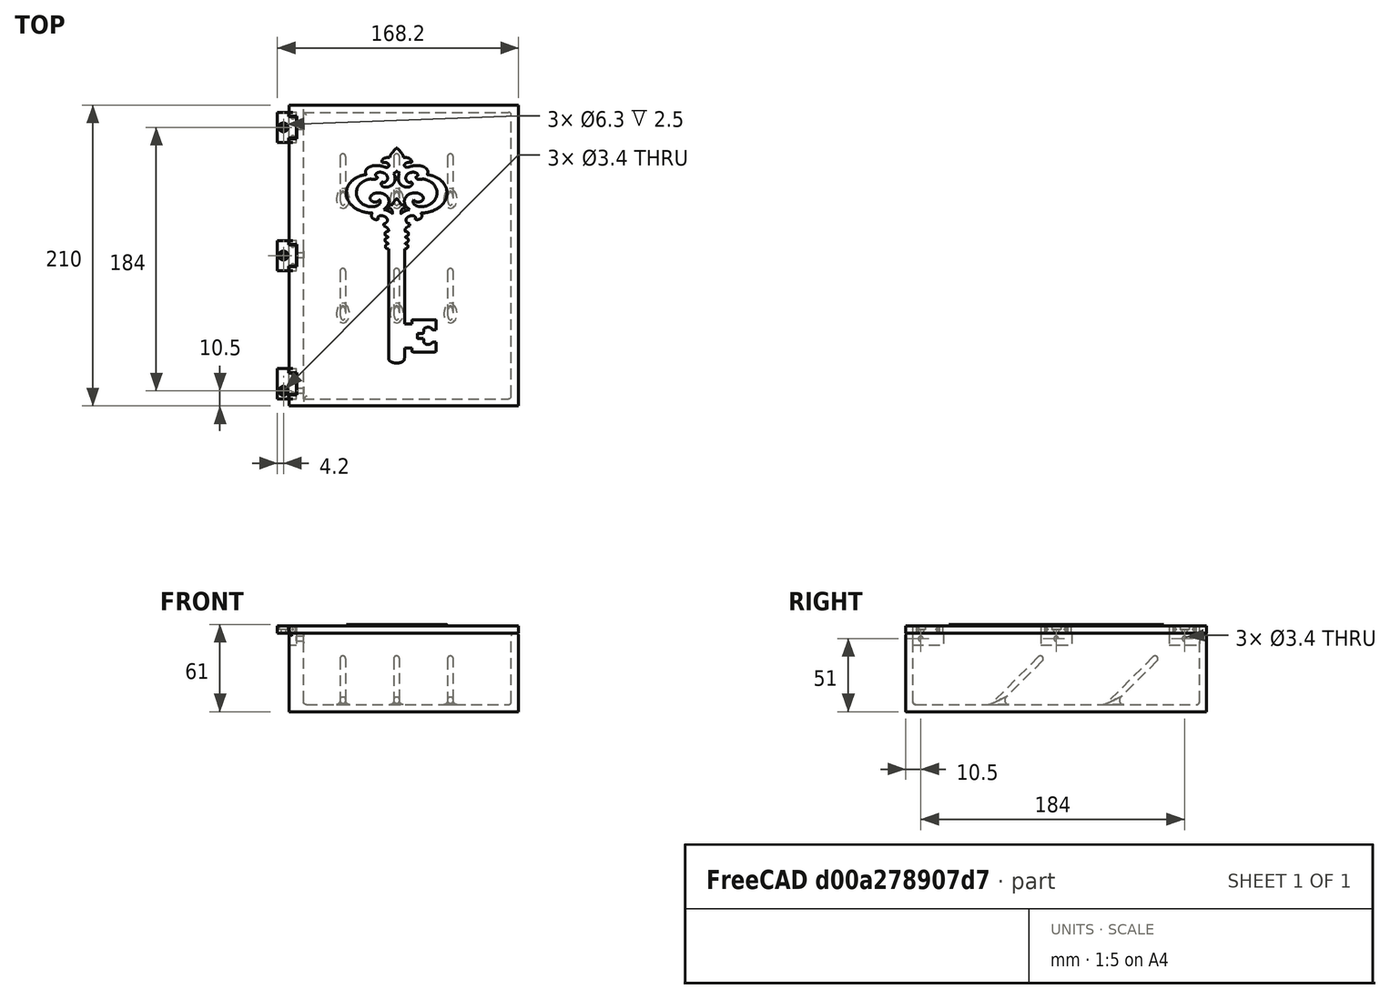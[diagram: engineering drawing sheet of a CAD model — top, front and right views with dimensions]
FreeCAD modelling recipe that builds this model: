
FCSTD DOCUMENT  (FreeCAD 1.1R1.1.0)
Label: SimpleCabinet
License: All rights reserved
LicenseURL: http://en.wikipedia.org/wiki/All_rights_reserved
objects: Part::MultiFuse×29, Part::Box×27, Part::Cylinder×24, Part::Cut×17, Part::Cone×12, Part::Fillet×4, Spreadsheet::Sheet×2, Part::Feature×1, App::Point×1, PartDesign::FeatureBase×1, PartDesign::Pad×1, PartDesign::Body×1
note: 120 computed .brp shape members not serialized (recipe doc carries the construction recipe); baked Part::Feature solids carry a one-line shape summary decoded from their .brp

FEATURE [Part::Box] Box  label="Cube"
  AttacherType = Attacher::AttachEngine3D
  Height = 50
  Length = 145
  Placement = pos=(10,5,5) rot=(0,0,1;0rad)
  Width = 200
  expr: .Placement.Base.x = <<Cabinet>>.wallthickness * 2
  expr: .Placement.Base.y = <<Cabinet>>.wallthickness
  expr: .Placement.Base.z = <<Cabinet>>.wallthickness
  expr: Height = <<Cabinet>>.depth
  expr: Length = <<Cabinet>>.width - <<Cabinet>>.wallthickness
  expr: Width = <<Cabinet>>.height
FEATURE [Spreadsheet::Sheet] Spreadsheet  label="Cabinet"
  cells = A2='Height; B2(height)=200; A3='Width; B3(width)=150; A4='Depth; B4(depth)=50; A5='Wall thickness; B5(wallthickness)=5
FEATURE [Part::Box] Box001  label="Cube001"
  AttacherType = Attacher::AttachEngine3D
  Height = 55
  Length = 160
  Width = 210
  expr: Height = <<Cabinet>>.depth + 1 * <<Cabinet>>.wallthickness
  expr: Length = <<Cabinet>>.width + 2 * <<Cabinet>>.wallthickness
  expr: Width = <<Cabinet>>.height + 2 * <<Cabinet>>.wallthickness
FEATURE [Part::Cut] Cut
  Base = -> Box001
  Tool = -> Box
FEATURE [Part::Box] Box002  label="Cube002"
  AttacherType = Attacher::AttachEngine3D
  Height = 5
  Length = 160
  Placement = pos=(0,0,55) rot=(0,0,1;0rad)
  Width = 210
  expr: .Placement.Base.z = <<Cabinet>>.depth + <<Cabinet>>.wallthickness
  expr: Height = <<Cabinet>>.wallthickness
  expr: Length = <<Cabinet>>.width + 2 * <<Cabinet>>.wallthickness
  expr: Width = <<Cabinet>>.height + 2 * <<Cabinet>>.wallthickness
FEATURE [Part::Box] Box003  label="Cube003"
  AttacherType = Attacher::AttachEngine3D
  Height = 5
  Length = 21
  Width = 10.9
  expr: Height = <<HingeParams>>.thickness
  expr: Length = <<HingeParams>>.h1 + <<HingeParams>>.h2
  expr: Width = <<HingeParams>>.e1 + <<HingeParams>>.thickness / 2 + <<HingeParams>>.gap
FEATURE [Part::Box] Box004  label="Cube004"
  AttacherType = Attacher::AttachEngine3D
  Height = 5
  Length = 15.8
  Placement = pos=(2.6,8,0) rot=(0,0,1;0rad)
  Width = 5.8
  expr: .Placement.Base.x = <<HingeParams>>.h2 / 2 - <<HingeParams>>.gap
  expr: .Placement.Base.y = <<HingeParams>>.e1
  expr: Height = <<HingeParams>>.thickness
  expr: Length = <<HingeParams>>.h1 + 2 * <<HingeParams>>.gap
  expr: Width = <<HingeParams>>.thickness + 2 * <<HingeParams>>.gap
FEATURE [Part::Box] Box005  label="Cube005"
  AttacherType = Attacher::AttachEngine3D
  Height = 5
  Length = 15
  Placement = pos=(3,10.9,0) rot=(0,0,1;0rad)
  Width = 10.5
  expr: .Placement.Base.x = <<HingeParams>>.h2 / 2
  expr: .Placement.Base.y = <<HingeParams>>.e1 + <<HingeParams>>.gap + <<HingeParams>>.thickness / 2
  expr: Height = <<HingeParams>>.thickness
  expr: Length = <<HingeParams>>.h1
  expr: Width = <<HingeParams>>.thickness / 2 + <<HingeParams>>.e2
FEATURE [Part::Box] Box006  label="Cube006"
  AttacherType = Attacher::AttachEngine3D
  Height = 5
  Length = 21
  Placement = pos=(0,13.8,0) rot=(0,0,1;0rad)
  Width = 7.8
  expr: .Placement.Base.y = <<HingeParams>>.e1 + <<HingeParams>>.thickness + <<HingeParams>>.gap * 2
  expr: Height = <<HingeParams>>.thickness
  expr: Length = <<HingeParams>>.h1 + <<HingeParams>>.h2
  expr: Width = <<HingeParams>>.e2 - <<HingeParams>>.gap / 2
FEATURE [Part::Cone] Cone
  Angle = 360
  AttacherType = Attacher::AttachEngine3D
  Height = 1.6
  Placement = pos=(4.2,10.9,2.5) rot=(0,1,0;-1.5708rad)
  Radius1 = 0.5
  Radius2 = 2.1
  expr: .Placement.Base.x = <<HingeParams>>.h2 / 2 - <<HingeParams>>.gap + <<HingeParams>>.thickness / 2 - <<HingeParams>>.gap - 0.5
  expr: .Placement.Base.y = <<HingeParams>>.e1 + <<HingeParams>>.gap + <<HingeParams>>.thickness / 2
  expr: .Placement.Base.z = <<HingeParams>>.thickness / 2
  expr: Height = <<HingeParams>>.thickness / 2 - <<HingeParams>>.gap - 0.5
  expr: Radius1 = 0.5
  expr: Radius2 = <<HingeParams>>.thickness / 2 - <<HingeParams>>.gap
FEATURE [Part::Cone] Cone002
  Angle = 360
  AttacherType = Attacher::AttachEngine3D
  Height = 2
  Placement = pos=(4.6,10.9,2.5) rot=(0,1,0;-1.5708rad)
  Radius1 = 0.5
  Radius2 = 2.5
  expr: .Placement.Base.x = <<HingeParams>>.h2 / 2 + <<HingeParams>>.thickness / 2 - <<HingeParams>>.gap - 0.5
  expr: .Placement.Base.y = <<HingeParams>>.e1 + <<HingeParams>>.gap + <<HingeParams>>.thickness / 2
  expr: .Placement.Base.z = <<HingeParams>>.thickness / 2
  expr: Height = <<HingeParams>>.thickness / 2 - 0.5
  expr: Radius1 = 0.5
  expr: Radius2 = <<HingeParams>>.thickness / 2
FEATURE [Part::Cone] Cone003
  Angle = 360
  AttacherType = Attacher::AttachEngine3D
  Height = 1.6
  Placement = pos=(16.8,10.9,2.5) rot=(0,1,0;1.5708rad)
  Radius1 = 0.5
  Radius2 = 2.1
  expr: .Placement.Base.x = <<HingeParams>>.h1 + <<HingeParams>>.h2 / 2 - (<<HingeParams>>.thickness / 2 - <<HingeParams>>.gap - 0.5) + <<HingeParams>>.gap
  expr: .Placement.Base.y = <<HingeParams>>.e1 + <<HingeParams>>.gap + <<HingeParams>>.thickness / 2
  expr: .Placement.Base.z = <<HingeParams>>.thickness / 2
  expr: Height = <<HingeParams>>.thickness / 2 - <<HingeParams>>.gap - 0.5
  expr: Radius1 = 0.5
  expr: Radius2 = <<HingeParams>>.thickness / 2 - <<HingeParams>>.gap
FEATURE [Part::Cone] Cone004
  Angle = 360
  AttacherType = Attacher::AttachEngine3D
  Height = 2
  Placement = pos=(16.4,10.9,2.5) rot=(0,1,0;1.5708rad)
  Radius1 = 0.5
  Radius2 = 2.5
  expr: .Placement.Base.x = <<HingeParams>>.h1 + <<HingeParams>>.h2 / 2 - (<<HingeParams>>.thickness / 2 - <<HingeParams>>.gap - 0.5)
  expr: .Placement.Base.y = <<HingeParams>>.e1 + <<HingeParams>>.gap + <<HingeParams>>.thickness / 2
  expr: .Placement.Base.z = <<HingeParams>>.thickness / 2
  expr: Height = <<HingeParams>>.thickness / 2 - 0.5
  expr: Radius1 = 0.5
  expr: Radius2 = <<HingeParams>>.thickness / 2
FEATURE [Part::Cylinder] Cylinder
  Angle = 360
  AttacherType = Attacher::AttachEngine3D
  FirstAngle = 0
  Height = 21
  Placement = pos=(0,10.9,2.5) rot=(0,1,0;1.5708rad)
  Radius = 2.5
  SecondAngle = 0
  expr: .Placement.Base.y = <<HingeParams>>.e1 + <<HingeParams>>.gap + <<HingeParams>>.thickness / 2
  expr: .Placement.Base.z = <<HingeParams>>.thickness / 2
  expr: Height = <<HingeParams>>.h1 + <<HingeParams>>.h2
  expr: Radius = <<HingeParams>>.thickness / 2
FEATURE [Part::Cylinder] Cylinder001
  Angle = 360
  AttacherType = Attacher::AttachEngine3D
  FirstAngle = 0
  Height = 15
  Placement = pos=(3,10.9,2.5) rot=(0,1,0;1.5708rad)
  Radius = 2.5
  SecondAngle = 0
  expr: .Placement.Base.x = <<HingeParams>>.h2 / 2
  expr: .Placement.Base.y = <<HingeParams>>.e1 + <<HingeParams>>.gap + <<HingeParams>>.thickness / 2
  expr: .Placement.Base.z = <<HingeParams>>.thickness / 2
  expr: Height = <<HingeParams>>.h1
  expr: Radius = <<HingeParams>>.thickness / 2
FEATURE [Part::MultiFuse] Fusion
  Shapes = -> [Box003,Cylinder]
FEATURE [Part::Cut] Cut001
  Base = -> Fusion
  Tool = -> Box004
FEATURE [Part::MultiFuse] Fusion001
  Shapes = -> [Cone,Cone003,Cut001]
FEATURE [Part::MultiFuse] Fusion002
  Shapes = -> [Box006,Box005,Cylinder001]
FEATURE [Part::MultiFuse] Fusion003
  Shapes = -> [Cone004,Cone002]
FEATURE [Part::Cut] Cut002
  Base = -> Fusion002
  Tool = -> Fusion003
FEATURE [Part::MultiFuse] Fusion004  label="Hinge"
  Placement = pos=(13.4,5,55) rot=(0,0,1;1.5708rad)
  Shapes = -> [Fusion001,Cut002]
  expr: .Placement.Base.x = 8 + <<Cabinet>>.wallthickness + <<HingeParams>>.gap
  expr: .Placement.Base.y = <<Cabinet>>.wallthickness
  expr: .Placement.Base.z = <<Cabinet>>.depth + <<Cabinet>>.wallthickness
FEATURE [Spreadsheet::Sheet] Spreadsheet001  label="HingeParams"
  cells = A2='Thickness; B2(thickness)==<<Cabinet>>.wallthickness; A3='Hinge length 1; B3(h1)=15; A4='Hinge length 2; B4(h2)=6; A5='Gap; B5(gap)=0.4; A6='Extend 1; B6(e1)=8; A7='Extend 2; B7(e2)=8
FEATURE [Part::Box] Box007  label="Cube007"
  AttacherType = Attacher::AttachEngine3D
  Height = 5
  Length = 13.4
  Placement = pos=(0,5,55) rot=(0,0,1;0rad)
  Width = 21
  expr: .Placement.Base.y = <<Cabinet>>.wallthickness
  expr: .Placement.Base.z = <<Cabinet>>.depth + <<Cabinet>>.wallthickness
  expr: Height = <<Cabinet>>.wallthickness
  expr: Length = 8 + <<HingeParams>>.gap + <<Cabinet>>.wallthickness
  expr: Width = <<HingeParams>>.h1 + <<HingeParams>>.h2
FEATURE [Part::Box] Box008  label="Cube008"
  AttacherType = Attacher::AttachEngine3D
  Height = 5
  Length = 13.4
  Placement = pos=(0,184,55) rot=(0,0,1;0rad)
  Width = 21
  expr: .Placement.Base.y = <<Cabinet>>.height + <<Cabinet>>.wallthickness * 2 - (<<HingeParams>>.h1 + <<HingeParams>>.h2) - <<Cabinet>>.wallthickness
  expr: .Placement.Base.z = <<Cabinet>>.depth + <<Cabinet>>.wallthickness
  expr: Height = <<Cabinet>>.wallthickness
  expr: Length = 8 + <<HingeParams>>.gap + <<Cabinet>>.wallthickness
  expr: Width = <<HingeParams>>.h1 + <<HingeParams>>.h2
FEATURE [Part::Box] Box009  label="Cube009"
  AttacherType = Attacher::AttachEngine3D
  Height = 5
  Length = 21
  Width = 10.9
  expr: Height = <<HingeParams>>.thickness
  expr: Length = <<HingeParams>>.h1 + <<HingeParams>>.h2
  expr: Width = <<HingeParams>>.e1 + <<HingeParams>>.thickness / 2 + <<HingeParams>>.gap
FEATURE [Part::Box] Box010  label="Cube010"
  AttacherType = Attacher::AttachEngine3D
  Height = 5
  Length = 15.8
  Placement = pos=(2.6,8,0) rot=(0,0,1;0rad)
  Width = 5.8
  expr: .Placement.Base.x = <<HingeParams>>.h2 / 2 - <<HingeParams>>.gap
  expr: .Placement.Base.y = <<HingeParams>>.e1
  expr: Height = <<HingeParams>>.thickness
  expr: Length = <<HingeParams>>.h1 + 2 * <<HingeParams>>.gap
  expr: Width = <<HingeParams>>.thickness + 2 * <<HingeParams>>.gap
FEATURE [Part::Box] Box011  label="Cube011"
  AttacherType = Attacher::AttachEngine3D
  Height = 5
  Length = 15
  Placement = pos=(3,10.9,0) rot=(0,0,1;0rad)
  Width = 10.5
  expr: .Placement.Base.x = <<HingeParams>>.h2 / 2
  expr: .Placement.Base.y = <<HingeParams>>.e1 + <<HingeParams>>.gap + <<HingeParams>>.thickness / 2
  expr: Height = <<HingeParams>>.thickness
  expr: Length = <<HingeParams>>.h1
  expr: Width = <<HingeParams>>.thickness / 2 + <<HingeParams>>.e2
FEATURE [Part::Box] Box012  label="Cube012"
  AttacherType = Attacher::AttachEngine3D
  Height = 5
  Length = 21
  Placement = pos=(0,13.8,0) rot=(0,0,1;0rad)
  Width = 7.8
  expr: .Placement.Base.y = <<HingeParams>>.e1 + <<HingeParams>>.thickness + <<HingeParams>>.gap * 2
  expr: Height = <<HingeParams>>.thickness
  expr: Length = <<HingeParams>>.h1 + <<HingeParams>>.h2
  expr: Width = <<HingeParams>>.e2 - <<HingeParams>>.gap / 2
FEATURE [Part::Cone] Cone005
  Angle = 360
  AttacherType = Attacher::AttachEngine3D
  Height = 1.6
  Placement = pos=(4.2,10.9,2.5) rot=(0,1,0;-1.5708rad)
  Radius1 = 0.5
  Radius2 = 2.1
  expr: .Placement.Base.x = <<HingeParams>>.h2 / 2 - <<HingeParams>>.gap + <<HingeParams>>.thickness / 2 - <<HingeParams>>.gap - 0.5
  expr: .Placement.Base.y = <<HingeParams>>.e1 + <<HingeParams>>.gap + <<HingeParams>>.thickness / 2
  expr: .Placement.Base.z = <<HingeParams>>.thickness / 2
  expr: Height = <<HingeParams>>.thickness / 2 - <<HingeParams>>.gap - 0.5
  expr: Radius1 = 0.5
  expr: Radius2 = <<HingeParams>>.thickness / 2 - <<HingeParams>>.gap
FEATURE [Part::Cone] Cone006
  Angle = 360
  AttacherType = Attacher::AttachEngine3D
  Height = 2
  Placement = pos=(4.6,10.9,2.5) rot=(0,1,0;-1.5708rad)
  Radius1 = 0.5
  Radius2 = 2.5
  expr: .Placement.Base.x = <<HingeParams>>.h2 / 2 + <<HingeParams>>.thickness / 2 - <<HingeParams>>.gap - 0.5
  expr: .Placement.Base.y = <<HingeParams>>.e1 + <<HingeParams>>.gap + <<HingeParams>>.thickness / 2
  expr: .Placement.Base.z = <<HingeParams>>.thickness / 2
  expr: Height = <<HingeParams>>.thickness / 2 - 0.5
  expr: Radius1 = 0.5
  expr: Radius2 = <<HingeParams>>.thickness / 2
FEATURE [Part::Cone] Cone007
  Angle = 360
  AttacherType = Attacher::AttachEngine3D
  Height = 1.6
  Placement = pos=(16.8,10.9,2.5) rot=(0,1,0;1.5708rad)
  Radius1 = 0.5
  Radius2 = 2.1
  expr: .Placement.Base.x = <<HingeParams>>.h1 + <<HingeParams>>.h2 / 2 - (<<HingeParams>>.thickness / 2 - <<HingeParams>>.gap - 0.5) + <<HingeParams>>.gap
  expr: .Placement.Base.y = <<HingeParams>>.e1 + <<HingeParams>>.gap + <<HingeParams>>.thickness / 2
  expr: .Placement.Base.z = <<HingeParams>>.thickness / 2
  expr: Height = <<HingeParams>>.thickness / 2 - <<HingeParams>>.gap - 0.5
  expr: Radius1 = 0.5
  expr: Radius2 = <<HingeParams>>.thickness / 2 - <<HingeParams>>.gap
FEATURE [Part::Cone] Cone008
  Angle = 360
  AttacherType = Attacher::AttachEngine3D
  Height = 2
  Placement = pos=(16.4,10.9,2.5) rot=(0,1,0;1.5708rad)
  Radius1 = 0.5
  Radius2 = 2.5
  expr: .Placement.Base.x = <<HingeParams>>.h1 + <<HingeParams>>.h2 / 2 - (<<HingeParams>>.thickness / 2 - <<HingeParams>>.gap - 0.5)
  expr: .Placement.Base.y = <<HingeParams>>.e1 + <<HingeParams>>.gap + <<HingeParams>>.thickness / 2
  expr: .Placement.Base.z = <<HingeParams>>.thickness / 2
  expr: Height = <<HingeParams>>.thickness / 2 - 0.5
  expr: Radius1 = 0.5
  expr: Radius2 = <<HingeParams>>.thickness / 2
FEATURE [Part::Cylinder] Cylinder002
  Angle = 360
  AttacherType = Attacher::AttachEngine3D
  FirstAngle = 0
  Height = 21
  Placement = pos=(0,10.9,2.5) rot=(0,1,0;1.5708rad)
  Radius = 2.5
  SecondAngle = 0
  expr: .Placement.Base.y = <<HingeParams>>.e1 + <<HingeParams>>.gap + <<HingeParams>>.thickness / 2
  expr: .Placement.Base.z = <<HingeParams>>.thickness / 2
  expr: Height = <<HingeParams>>.h1 + <<HingeParams>>.h2
  expr: Radius = <<HingeParams>>.thickness / 2
FEATURE [Part::Cylinder] Cylinder003
  Angle = 360
  AttacherType = Attacher::AttachEngine3D
  FirstAngle = 0
  Height = 15
  Placement = pos=(3,10.9,2.5) rot=(0,1,0;1.5708rad)
  Radius = 2.5
  SecondAngle = 0
  expr: .Placement.Base.x = <<HingeParams>>.h2 / 2
  expr: .Placement.Base.y = <<HingeParams>>.e1 + <<HingeParams>>.gap + <<HingeParams>>.thickness / 2
  expr: .Placement.Base.z = <<HingeParams>>.thickness / 2
  expr: Height = <<HingeParams>>.h1
  expr: Radius = <<HingeParams>>.thickness / 2
FEATURE [Part::MultiFuse] Fusion005
  Shapes = -> [Box009,Cylinder002]
FEATURE [Part::Cut] Cut003
  Base = -> Fusion005
  Tool = -> Box010
FEATURE [Part::MultiFuse] Fusion006
  Shapes = -> [Cone005,Cone007,Cut003]
FEATURE [Part::MultiFuse] Fusion007
  Shapes = -> [Box012,Box011,Cylinder003]
FEATURE [Part::MultiFuse] Fusion008
  Shapes = -> [Cone008,Cone006]
FEATURE [Part::Cut] Cut004
  Base = -> Fusion007
  Tool = -> Fusion008
FEATURE [Part::MultiFuse] Fusion009  label="Hinge001"
  Placement = pos=(13.4,184,55) rot=(0,0,1;1.5708rad)
  Shapes = -> [Fusion006,Cut004]
  expr: .Placement.Base.x = 8 + <<Cabinet>>.wallthickness + <<HingeParams>>.gap
  expr: .Placement.Base.y = <<Cabinet>>.height + <<Cabinet>>.wallthickness * 2 - (<<HingeParams>>.h1 + <<HingeParams>>.h2) - <<Cabinet>>.wallthickness
  expr: .Placement.Base.z = <<Cabinet>>.depth + <<Cabinet>>.wallthickness
FEATURE [Part::Box] Box013  label="Cube013"
  AttacherType = Attacher::AttachEngine3D
  Height = 5
  Length = 13.4
  Placement = pos=(0,94.5,55) rot=(0,0,1;0rad)
  Width = 21
  expr: .Placement.Base.y = <<Cabinet>>.height / 2 + <<Cabinet>>.wallthickness - (<<HingeParams>>.h1 + <<HingeParams>>.h2) / 2
  expr: .Placement.Base.z = <<Cabinet>>.depth + <<Cabinet>>.wallthickness
  expr: Height = <<Cabinet>>.wallthickness
  expr: Length = 8 + <<HingeParams>>.gap + <<Cabinet>>.wallthickness
  expr: Width = <<HingeParams>>.h1 + <<HingeParams>>.h2
FEATURE [Part::Box] Box014  label="Cube014"
  AttacherType = Attacher::AttachEngine3D
  Height = 5
  Length = 21
  Width = 10.9
  expr: Height = <<HingeParams>>.thickness
  expr: Length = <<HingeParams>>.h1 + <<HingeParams>>.h2
  expr: Width = <<HingeParams>>.e1 + <<HingeParams>>.thickness / 2 + <<HingeParams>>.gap
FEATURE [Part::Box] Box015  label="Cube015"
  AttacherType = Attacher::AttachEngine3D
  Height = 5
  Length = 15.8
  Placement = pos=(2.6,8,0) rot=(0,0,1;0rad)
  Width = 5.8
  expr: .Placement.Base.x = <<HingeParams>>.h2 / 2 - <<HingeParams>>.gap
  expr: .Placement.Base.y = <<HingeParams>>.e1
  expr: Height = <<HingeParams>>.thickness
  expr: Length = <<HingeParams>>.h1 + 2 * <<HingeParams>>.gap
  expr: Width = <<HingeParams>>.thickness + 2 * <<HingeParams>>.gap
FEATURE [Part::Box] Box016  label="Cube016"
  AttacherType = Attacher::AttachEngine3D
  Height = 5
  Length = 15
  Placement = pos=(3,10.9,0) rot=(0,0,1;0rad)
  Width = 10.5
  expr: .Placement.Base.x = <<HingeParams>>.h2 / 2
  expr: .Placement.Base.y = <<HingeParams>>.e1 + <<HingeParams>>.gap + <<HingeParams>>.thickness / 2
  expr: Height = <<HingeParams>>.thickness
  expr: Length = <<HingeParams>>.h1
  expr: Width = <<HingeParams>>.thickness / 2 + <<HingeParams>>.e2
FEATURE [Part::Box] Box017  label="Cube017"
  AttacherType = Attacher::AttachEngine3D
  Height = 5
  Length = 21
  Placement = pos=(0,13.8,0) rot=(0,0,1;0rad)
  Width = 7.8
  expr: .Placement.Base.y = <<HingeParams>>.e1 + <<HingeParams>>.thickness + <<HingeParams>>.gap * 2
  expr: Height = <<HingeParams>>.thickness
  expr: Length = <<HingeParams>>.h1 + <<HingeParams>>.h2
  expr: Width = <<HingeParams>>.e2 - <<HingeParams>>.gap / 2
FEATURE [Part::Cone] Cone009
  Angle = 360
  AttacherType = Attacher::AttachEngine3D
  Height = 1.6
  Placement = pos=(4.2,10.9,2.5) rot=(0,1,0;-1.5708rad)
  Radius1 = 0.5
  Radius2 = 2.1
  expr: .Placement.Base.x = <<HingeParams>>.h2 / 2 - <<HingeParams>>.gap + <<HingeParams>>.thickness / 2 - <<HingeParams>>.gap - 0.5
  expr: .Placement.Base.y = <<HingeParams>>.e1 + <<HingeParams>>.gap + <<HingeParams>>.thickness / 2
  expr: .Placement.Base.z = <<HingeParams>>.thickness / 2
  expr: Height = <<HingeParams>>.thickness / 2 - <<HingeParams>>.gap - 0.5
  expr: Radius1 = 0.5
  expr: Radius2 = <<HingeParams>>.thickness / 2 - <<HingeParams>>.gap
FEATURE [Part::Cone] Cone010
  Angle = 360
  AttacherType = Attacher::AttachEngine3D
  Height = 2
  Placement = pos=(4.6,10.9,2.5) rot=(0,1,0;-1.5708rad)
  Radius1 = 0.5
  Radius2 = 2.5
  expr: .Placement.Base.x = <<HingeParams>>.h2 / 2 + <<HingeParams>>.thickness / 2 - <<HingeParams>>.gap - 0.5
  expr: .Placement.Base.y = <<HingeParams>>.e1 + <<HingeParams>>.gap + <<HingeParams>>.thickness / 2
  expr: .Placement.Base.z = <<HingeParams>>.thickness / 2
  expr: Height = <<HingeParams>>.thickness / 2 - 0.5
  expr: Radius1 = 0.5
  expr: Radius2 = <<HingeParams>>.thickness / 2
FEATURE [Part::Cone] Cone011
  Angle = 360
  AttacherType = Attacher::AttachEngine3D
  Height = 1.6
  Placement = pos=(16.8,10.9,2.5) rot=(0,1,0;1.5708rad)
  Radius1 = 0.5
  Radius2 = 2.1
  expr: .Placement.Base.x = <<HingeParams>>.h1 + <<HingeParams>>.h2 / 2 - (<<HingeParams>>.thickness / 2 - <<HingeParams>>.gap - 0.5) + <<HingeParams>>.gap
  expr: .Placement.Base.y = <<HingeParams>>.e1 + <<HingeParams>>.gap + <<HingeParams>>.thickness / 2
  expr: .Placement.Base.z = <<HingeParams>>.thickness / 2
  expr: Height = <<HingeParams>>.thickness / 2 - <<HingeParams>>.gap - 0.5
  expr: Radius1 = 0.5
  expr: Radius2 = <<HingeParams>>.thickness / 2 - <<HingeParams>>.gap
FEATURE [Part::Cone] Cone012
  Angle = 360
  AttacherType = Attacher::AttachEngine3D
  Height = 2
  Placement = pos=(16.4,10.9,2.5) rot=(0,1,0;1.5708rad)
  Radius1 = 0.5
  Radius2 = 2.5
  expr: .Placement.Base.x = <<HingeParams>>.h1 + <<HingeParams>>.h2 / 2 - (<<HingeParams>>.thickness / 2 - <<HingeParams>>.gap - 0.5)
  expr: .Placement.Base.y = <<HingeParams>>.e1 + <<HingeParams>>.gap + <<HingeParams>>.thickness / 2
  expr: .Placement.Base.z = <<HingeParams>>.thickness / 2
  expr: Height = <<HingeParams>>.thickness / 2 - 0.5
  expr: Radius1 = 0.5
  expr: Radius2 = <<HingeParams>>.thickness / 2
FEATURE [Part::Cylinder] Cylinder004
  Angle = 360
  AttacherType = Attacher::AttachEngine3D
  FirstAngle = 0
  Height = 21
  Placement = pos=(0,10.9,2.5) rot=(0,1,0;1.5708rad)
  Radius = 2.5
  SecondAngle = 0
  expr: .Placement.Base.y = <<HingeParams>>.e1 + <<HingeParams>>.gap + <<HingeParams>>.thickness / 2
  expr: .Placement.Base.z = <<HingeParams>>.thickness / 2
  expr: Height = <<HingeParams>>.h1 + <<HingeParams>>.h2
  expr: Radius = <<HingeParams>>.thickness / 2
FEATURE [Part::Cylinder] Cylinder005
  Angle = 360
  AttacherType = Attacher::AttachEngine3D
  FirstAngle = 0
  Height = 15
  Placement = pos=(3,10.9,2.5) rot=(0,1,0;1.5708rad)
  Radius = 2.5
  SecondAngle = 0
  expr: .Placement.Base.x = <<HingeParams>>.h2 / 2
  expr: .Placement.Base.y = <<HingeParams>>.e1 + <<HingeParams>>.gap + <<HingeParams>>.thickness / 2
  expr: .Placement.Base.z = <<HingeParams>>.thickness / 2
  expr: Height = <<HingeParams>>.h1
  expr: Radius = <<HingeParams>>.thickness / 2
FEATURE [Part::MultiFuse] Fusion010
  Shapes = -> [Box014,Cylinder004]
FEATURE [Part::Cut] Cut005
  Base = -> Fusion010
  Tool = -> Box015
FEATURE [Part::MultiFuse] Fusion011
  Shapes = -> [Cone009,Cone011,Cut005]
FEATURE [Part::MultiFuse] Fusion012
  Shapes = -> [Box017,Box016,Cylinder005]
FEATURE [Part::MultiFuse] Fusion013
  Shapes = -> [Cone012,Cone010]
FEATURE [Part::Cut] Cut006
  Base = -> Fusion012
  Tool = -> Fusion013
FEATURE [Part::MultiFuse] Fusion014  label="Hinge002"
  Placement = pos=(13.4,94.5,55) rot=(0,0,1;1.5708rad)
  Shapes = -> [Fusion011,Cut006]
  expr: .Placement.Base.x = 8 + <<Cabinet>>.wallthickness + <<HingeParams>>.gap
  expr: .Placement.Base.y = <<Cabinet>>.height / 2 + <<Cabinet>>.wallthickness - (<<HingeParams>>.h1 + <<HingeParams>>.h2) / 2
  expr: .Placement.Base.z = <<Cabinet>>.depth + <<Cabinet>>.wallthickness
FEATURE [Part::MultiFuse] Fusion015
  Shapes = -> [Box007,Box008,Box013]
FEATURE [Part::Cut] Cut007
  Base = -> Box002
  Tool = -> Fusion015
FEATURE [Part::MultiFuse] Fusion016
  Shapes = -> [Cut007,Fusion014,Fusion009,Fusion004]
FEATURE [Part::Feature] path1
  shape: bbox 70.04 x 150 x 2e-07 mm, 1 faces, 0 solids (baked)
FEATURE [App::Point] Origin001
  Role = Origin
FEATURE [PartDesign::FeatureBase] BaseFeature
  BaseFeature = -> path1
  Suppressed = false
FEATURE [PartDesign::Pad] Pad
  BaseFeature = -> BaseFeature
  Direction = (0,0,-1)
  Length = 1
  Length2 = 10
  Profile = -> BaseFeature
  SideType = 0
  Suppressed = false
  Type = 0
  Type2 = 0
  expr: Length = 1
FEATURE [PartDesign::Body] Body  label="KeySymbol"
  AllowCompound = false
  BaseFeature = -> path1
  Group = -> [BaseFeature,Pad]
  Origin = -> Origin
  Placement = pos=(40,180,61) rot=(0,0,1;0rad)
  Tip = -> Pad
  expr: .Placement.Base.x = <<Cabinet>>.width / 2 - 35
  expr: .Placement.Base.y = <<Cabinet>>.height / 2 + <<Cabinet>>.wallthickness + 150 / 2
  expr: .Placement.Base.z = <<Cabinet>>.wallthickness + <<Cabinet>>.depth + <<Cabinet>>.wallthickness + 1
FEATURE [Part::Box] Box018  label="Cube018"
  AttacherType = Attacher::AttachEngine3D
  Height = 5
  Length = 8.4
  Placement = pos=(0,4.8,55) rot=(0,0,1;0rad)
  Width = 21.4
  expr: .Placement.Base.y = <<Cabinet>>.wallthickness - 0.2
  expr: .Placement.Base.z = <<Cabinet>>.depth + <<Cabinet>>.wallthickness
  expr: Height = <<Cabinet>>.wallthickness
  expr: Length = 8 + 0.4
  expr: Width = <<HingeParams>>.h1 + <<HingeParams>>.h2 + 0.4
FEATURE [Part::Box] Box019  label="Cube019"
  AttacherType = Attacher::AttachEngine3D
  Height = 5
  Length = 8.4
  Placement = pos=(0,183.8,55) rot=(0,0,1;0rad)
  Width = 21.4
  expr: .Placement.Base.y = <<Cabinet>>.height + <<Cabinet>>.wallthickness * 2 - (<<HingeParams>>.h1 + <<HingeParams>>.h2) - <<Cabinet>>.wallthickness - 0.2
  expr: .Placement.Base.z = <<Cabinet>>.depth + <<Cabinet>>.wallthickness
  expr: Height = <<Cabinet>>.wallthickness
  expr: Length = 8 + 0.4
  expr: Width = <<HingeParams>>.h1 + <<HingeParams>>.h2 + 0.4
FEATURE [Part::Box] Box020  label="Cube020"
  AttacherType = Attacher::AttachEngine3D
  Height = 5
  Length = 8.4
  Placement = pos=(0,94.3,55) rot=(0,0,1;0rad)
  Width = 21.4
  expr: .Placement.Base.y = <<Cabinet>>.height / 2 + <<Cabinet>>.wallthickness - (<<HingeParams>>.h1 + <<HingeParams>>.h2) / 2 - 0.2
  expr: .Placement.Base.z = <<Cabinet>>.depth + <<Cabinet>>.wallthickness
  expr: Height = <<Cabinet>>.wallthickness
  expr: Length = 8 + 0.4
  expr: Width = <<HingeParams>>.h1 + <<HingeParams>>.h2 + 0.4
FEATURE [Part::MultiFuse] Fusion017
  Placement = pos=(-55,0,55) rot=(0,1,0;1.5708rad)
  Shapes = -> [Box018,Box019,Box020]
  expr: .Placement.Base.x = -<<Cabinet>>.depth - <<Cabinet>>.wallthickness
  expr: .Placement.Base.z = <<Cabinet>>.depth + <<Cabinet>>.wallthickness
FEATURE [Part::Cylinder] Cylinder006
  Angle = 360
  AttacherType = Attacher::AttachEngine3D
  FirstAngle = 0
  Height = 10
  Placement = pos=(-4,10.5,50) rot=(0,0,1;0rad)
  Radius = 1.7
  SecondAngle = 0
  expr: .Placement.Base.y = (<<HingeParams>>.h1 + <<HingeParams>>.h2) / 2
  expr: .Placement.Base.z = <<Cabinet>>.depth
FEATURE [Part::Cylinder] Cylinder007
  Angle = 360
  AttacherType = Attacher::AttachEngine3D
  FirstAngle = 0
  Height = 10
  Placement = pos=(-4,10.5,57.5) rot=(0,0,1;0rad)
  Radius = 3.15
  SecondAngle = 0
  expr: .Placement.Base.y = (<<HingeParams>>.h1 + <<HingeParams>>.h2) / 2
  expr: .Placement.Base.z = <<Cabinet>>.depth + <<Cabinet>>.wallthickness + <<Cabinet>>.wallthickness / 2
FEATURE [Part::MultiFuse] Fusion018
  Shapes = -> [Cylinder006,Cylinder007]
FEATURE [Part::Cylinder] Cylinder008
  Angle = 360
  AttacherType = Attacher::AttachEngine3D
  FirstAngle = 0
  Height = 10
  Placement = pos=(-4,10.5,50) rot=(0,0,1;0rad)
  Radius = 1.7
  SecondAngle = 0
  expr: .Placement.Base.y = (<<HingeParams>>.h1 + <<HingeParams>>.h2) / 2
  expr: .Placement.Base.z = <<Cabinet>>.depth
FEATURE [Part::Cylinder] Cylinder009
  Angle = 360
  AttacherType = Attacher::AttachEngine3D
  FirstAngle = 0
  Height = 10
  Placement = pos=(-4,10.5,57.5) rot=(0,0,1;0rad)
  Radius = 3.15
  SecondAngle = 0
  expr: .Placement.Base.y = (<<HingeParams>>.h1 + <<HingeParams>>.h2) / 2
  expr: .Placement.Base.z = <<Cabinet>>.depth + <<Cabinet>>.wallthickness + <<Cabinet>>.wallthickness / 2
FEATURE [Part::MultiFuse] Fusion019
  Placement = pos=(0,184,0) rot=(0,0,1;0rad)
  Shapes = -> [Cylinder008,Cylinder009]
  expr: .Placement.Base.y = <<Cabinet>>.height + <<Cabinet>>.wallthickness * 2 - (<<HingeParams>>.h1 + <<HingeParams>>.h2) - <<Cabinet>>.wallthickness
FEATURE [Part::Cylinder] Cylinder010
  Angle = 360
  AttacherType = Attacher::AttachEngine3D
  FirstAngle = 0
  Height = 10
  Placement = pos=(-4,10.5,50) rot=(0,0,1;0rad)
  Radius = 1.7
  SecondAngle = 0
  expr: .Placement.Base.y = (<<HingeParams>>.h1 + <<HingeParams>>.h2) / 2
  expr: .Placement.Base.z = <<Cabinet>>.depth
FEATURE [Part::Cylinder] Cylinder011
  Angle = 360
  AttacherType = Attacher::AttachEngine3D
  FirstAngle = 0
  Height = 10
  Placement = pos=(-4,10.5,57.5) rot=(0,0,1;0rad)
  Radius = 3.15
  SecondAngle = 0
  expr: .Placement.Base.y = (<<HingeParams>>.h1 + <<HingeParams>>.h2) / 2
  expr: .Placement.Base.z = <<Cabinet>>.depth + <<Cabinet>>.wallthickness + <<Cabinet>>.wallthickness / 2
FEATURE [Part::MultiFuse] Fusion020
  Placement = pos=(0,94.5,0) rot=(0,0,1;0rad)
  Shapes = -> [Cylinder010,Cylinder011]
  expr: .Placement.Base.y = <<Cabinet>>.height / 2 + <<Cabinet>>.wallthickness - (<<HingeParams>>.h1 + <<HingeParams>>.h2) / 2
FEATURE [Part::MultiFuse] Fusion021
  Shapes = -> [Fusion018,Fusion019,Fusion020]
FEATURE [Part::Cut] Cut008
  Base = -> Fusion016
  Tool = -> Fusion021
FEATURE [Part::MultiFuse] Fusion022  label="Front"
  Shapes = -> [Cut008,Body]
FEATURE [Part::Cylinder] Cylinder013
  Angle = 360
  AttacherType = Attacher::AttachEngine3D
  FirstAngle = 0
  Height = 10
  Placement = pos=(-4,10.5,50) rot=(0,0,1;0rad)
  Radius = 1.7
  SecondAngle = 0
  expr: .Placement.Base.y = (<<HingeParams>>.h1 + <<HingeParams>>.h2) / 2
  expr: .Placement.Base.z = <<Cabinet>>.depth
FEATURE [Part::Cylinder] Cylinder014
  Angle = 360
  AttacherType = Attacher::AttachEngine3D
  FirstAngle = 0
  Height = 10
  Placement = pos=(-4,10.5,60) rot=(0,0,1;0rad)
  Radius = 3.15
  SecondAngle = 0
  expr: .Placement.Base.y = (<<HingeParams>>.h1 + <<HingeParams>>.h2) / 2
  expr: .Placement.Base.z = <<Cabinet>>.depth + <<Cabinet>>.wallthickness + <<Cabinet>>.wallthickness
FEATURE [Part::Cylinder] Cylinder015
  Angle = 360
  AttacherType = Attacher::AttachEngine3D
  FirstAngle = 0
  Height = 10
  Placement = pos=(-4,10.5,50) rot=(0,0,1;0rad)
  Radius = 1.7
  SecondAngle = 0
  expr: .Placement.Base.y = (<<HingeParams>>.h1 + <<HingeParams>>.h2) / 2
  expr: .Placement.Base.z = <<Cabinet>>.depth
FEATURE [Part::Cylinder] Cylinder016
  Angle = 360
  AttacherType = Attacher::AttachEngine3D
  FirstAngle = 0
  Height = 10
  Placement = pos=(-4,10.5,60) rot=(0,0,1;0rad)
  Radius = 3.15
  SecondAngle = 0
  expr: .Placement.Base.y = (<<HingeParams>>.h1 + <<HingeParams>>.h2) / 2
  expr: .Placement.Base.z = <<Cabinet>>.depth + <<Cabinet>>.wallthickness + <<Cabinet>>.wallthickness
FEATURE [Part::Cylinder] Cylinder017
  Angle = 360
  AttacherType = Attacher::AttachEngine3D
  FirstAngle = 0
  Height = 10
  Placement = pos=(-4,10.5,50) rot=(0,0,1;0rad)
  Radius = 1.7
  SecondAngle = 0
  expr: .Placement.Base.y = (<<HingeParams>>.h1 + <<HingeParams>>.h2) / 2
  expr: .Placement.Base.z = <<Cabinet>>.depth
FEATURE [Part::Cylinder] Cylinder018
  Angle = 360
  AttacherType = Attacher::AttachEngine3D
  FirstAngle = 0
  Height = 10
  Placement = pos=(-4,10.5,60) rot=(0,0,1;0rad)
  Radius = 3.15
  SecondAngle = 0
  expr: .Placement.Base.y = (<<HingeParams>>.h1 + <<HingeParams>>.h2) / 2
  expr: .Placement.Base.z = <<Cabinet>>.depth + <<Cabinet>>.wallthickness + <<Cabinet>>.wallthickness
FEATURE [Part::MultiFuse] Fusion023
  Shapes = -> [Cylinder013,Cylinder014]
FEATURE [Part::MultiFuse] Fusion024
  Placement = pos=(0,184,0) rot=(0,0,1;0rad)
  Shapes = -> [Cylinder015,Cylinder016]
  expr: .Placement.Base.y = <<Cabinet>>.height + <<Cabinet>>.wallthickness * 2 - (<<HingeParams>>.h1 + <<HingeParams>>.h2) - <<Cabinet>>.wallthickness
FEATURE [Part::MultiFuse] Fusion025
  Placement = pos=(0,94.5,0) rot=(0,0,1;0rad)
  Shapes = -> [Cylinder017,Cylinder018]
  expr: .Placement.Base.y = <<Cabinet>>.height / 2 + <<Cabinet>>.wallthickness - (<<HingeParams>>.h1 + <<HingeParams>>.h2) / 2
FEATURE [Part::MultiFuse] Fusion026
  Placement = pos=(-50,0,47) rot=(0,1,0;1.5708rad)
  Shapes = -> [Fusion023,Fusion024,Fusion025]
  expr: .Placement.Base.x = -<<Cabinet>>.depth
  expr: .Placement.Base.z = <<Cabinet>>.depth + <<Cabinet>>.wallthickness - 8
FEATURE [Part::Cut] Cut009
  Base = -> Cut
  Tool = -> Fusion017
FEATURE [Part::Cut] Cut010
  Base = -> Cut009
  Tool = -> Fusion026
FEATURE [Part::Cylinder] Cylinder019
  Angle = 360
  AttacherType = Attacher::AttachEngine3D
  FirstAngle = 0
  Height = 50
  Placement = pos=(0,0,-2) rot=(1,0,0;-0.785398rad)
  Radius = 2
  SecondAngle = 0
  expr: Height = <<Cabinet>>.depth
FEATURE [Part::Box] Box021  label="Cube021"
  AttacherType = Attacher::AttachEngine3D
  Height = 10
  Length = 10
  Placement = pos=(-5,-5,-10) rot=(0,0,1;0rad)
  Width = 10
FEATURE [Part::Cut] Cut011
  Base = -> Cylinder019
  Placement = pos=(37.5,60,5) rot=(0,0,1;0rad)
  Tool = -> Box021
  expr: .Placement.Base.x = <<Cabinet>>.width * 1 / 4
  expr: .Placement.Base.y = <<Cabinet>>.height * 0.3
  expr: .Placement.Base.z = <<Cabinet>>.wallthickness
FEATURE [Part::Box] Box022  label="Cube022"
  AttacherType = Attacher::AttachEngine3D
  Height = 10
  Length = 10
  Placement = pos=(-5,-5,-10) rot=(0,0,1;0rad)
  Width = 10
FEATURE [Part::Cylinder] Cylinder020
  Angle = 360
  AttacherType = Attacher::AttachEngine3D
  FirstAngle = 0
  Height = 50
  Placement = pos=(0,0,-2) rot=(1,0,0;-0.785398rad)
  Radius = 2
  SecondAngle = 0
  expr: Height = <<Cabinet>>.depth
FEATURE [Part::Cut] Cut012
  Base = -> Cylinder020
  Placement = pos=(37.5,140,5) rot=(0,0,1;0rad)
  Tool = -> Box022
  expr: .Placement.Base.x = <<Cabinet>>.width * 1 / 4
  expr: .Placement.Base.y = <<Cabinet>>.height * 0.7
  expr: .Placement.Base.z = <<Cabinet>>.wallthickness
FEATURE [Part::Box] Box023  label="Cube023"
  AttacherType = Attacher::AttachEngine3D
  Height = 10
  Length = 10
  Placement = pos=(-5,-5,-10) rot=(0,0,1;0rad)
  Width = 10
FEATURE [Part::Cylinder] Cylinder021
  Angle = 360
  AttacherType = Attacher::AttachEngine3D
  FirstAngle = 0
  Height = 50
  Placement = pos=(0,0,-2) rot=(1,0,0;-0.785398rad)
  Radius = 2
  SecondAngle = 0
  expr: Height = <<Cabinet>>.depth
FEATURE [Part::Cut] Cut013
  Base = -> Cylinder021
  Placement = pos=(75,60,5) rot=(0,0,1;0rad)
  Tool = -> Box023
  expr: .Placement.Base.x = <<Cabinet>>.width * 2 / 4
  expr: .Placement.Base.y = <<Cabinet>>.height * 0.3
  expr: .Placement.Base.z = <<Cabinet>>.wallthickness
FEATURE [Part::Box] Box024  label="Cube024"
  AttacherType = Attacher::AttachEngine3D
  Height = 10
  Length = 10
  Placement = pos=(-5,-5,-10) rot=(0,0,1;0rad)
  Width = 10
FEATURE [Part::Cylinder] Cylinder022
  Angle = 360
  AttacherType = Attacher::AttachEngine3D
  FirstAngle = 0
  Height = 50
  Placement = pos=(0,0,-2) rot=(1,0,0;-0.785398rad)
  Radius = 2
  SecondAngle = 0
  expr: Height = <<Cabinet>>.depth
FEATURE [Part::Cut] Cut014
  Base = -> Cylinder022
  Placement = pos=(112.5,60,5) rot=(0,0,1;0rad)
  Tool = -> Box024
  expr: .Placement.Base.x = <<Cabinet>>.width * 3 / 4
  expr: .Placement.Base.y = <<Cabinet>>.height * 0.3
  expr: .Placement.Base.z = <<Cabinet>>.wallthickness
FEATURE [Part::Box] Box025  label="Cube025"
  AttacherType = Attacher::AttachEngine3D
  Height = 10
  Length = 10
  Placement = pos=(-5,-5,-10) rot=(0,0,1;0rad)
  Width = 10
FEATURE [Part::Cylinder] Cylinder023
  Angle = 360
  AttacherType = Attacher::AttachEngine3D
  FirstAngle = 0
  Height = 50
  Placement = pos=(0,0,-2) rot=(1,0,0;-0.785398rad)
  Radius = 2
  SecondAngle = 0
  expr: Height = <<Cabinet>>.depth
FEATURE [Part::Cut] Cut015
  Base = -> Cylinder023
  Placement = pos=(75,140,5) rot=(0,0,1;0rad)
  Tool = -> Box025
  expr: .Placement.Base.x = <<Cabinet>>.width * 2 / 4
  expr: .Placement.Base.y = <<Cabinet>>.height * 0.7
  expr: .Placement.Base.z = <<Cabinet>>.wallthickness
FEATURE [Part::Box] Box026  label="Cube026"
  AttacherType = Attacher::AttachEngine3D
  Height = 10
  Length = 10
  Placement = pos=(-5,-5,-10) rot=(0,0,1;0rad)
  Width = 10
FEATURE [Part::Cylinder] Cylinder024
  Angle = 360
  AttacherType = Attacher::AttachEngine3D
  FirstAngle = 0
  Height = 50
  Placement = pos=(0,0,-2) rot=(1,0,0;-0.785398rad)
  Radius = 2
  SecondAngle = 0
  expr: Height = <<Cabinet>>.depth
FEATURE [Part::Cut] Cut016
  Base = -> Cylinder024
  Placement = pos=(112.5,140,5) rot=(0,0,1;0rad)
  Tool = -> Box026
  expr: .Placement.Base.x = <<Cabinet>>.width * 3 / 4
  expr: .Placement.Base.y = <<Cabinet>>.height * 0.7
  expr: .Placement.Base.z = <<Cabinet>>.wallthickness
FEATURE [Part::MultiFuse] Fusion027
  Shapes = -> [Cut011,Cut012,Cut013,Cut014,Cut015,Cut016]
FEATURE [Part::MultiFuse] Fusion028
  Shapes = -> [Cut010,Fusion027]
FEATURE [Part::Fillet] Fillet
  Base = -> Fusion028
  EdgeLinks = -> Fusion028 [Edge73,Edge74,Edge75,Edge76,Edge77,Edge78]
  Edges = 6 edges r=3: [Edge73,Edge74,Edge75,Edge76,Edge77,Edge78]
FEATURE [Part::Fillet] Fillet001
  Base = -> Fillet
  EdgeLinks = -> Fillet [Edge2,Edge3,Edge4,Edge5,Edge19,Edge21]
  Edges = 6 edges r=2: [Edge2,Edge3,Edge4,Edge5,Edge19,Edge21]
FEATURE [Part::Fillet] Fillet002
  Base = -> Fillet001
  EdgeLinks = -> Fillet001 [Edge39,Edge47,Edge77,Edge78,Edge79,Edge92,Edge94,Edge114,Edge115]
  Edges = 9 edges r=2: [Edge39,Edge47,Edge77,Edge78,Edge79,Edge92,Edge94,Edge114,Edge115]
FEATURE [Part::Fillet] Fillet003
  Base = -> Fillet002
  EdgeLinks = -> Fillet002 [Edge144,Edge146,Edge148,Edge150,Edge152,Edge154]
  Edges = 6 edges r=2: [Edge144,Edge146,Edge148,Edge150,Edge152,Edge154]
